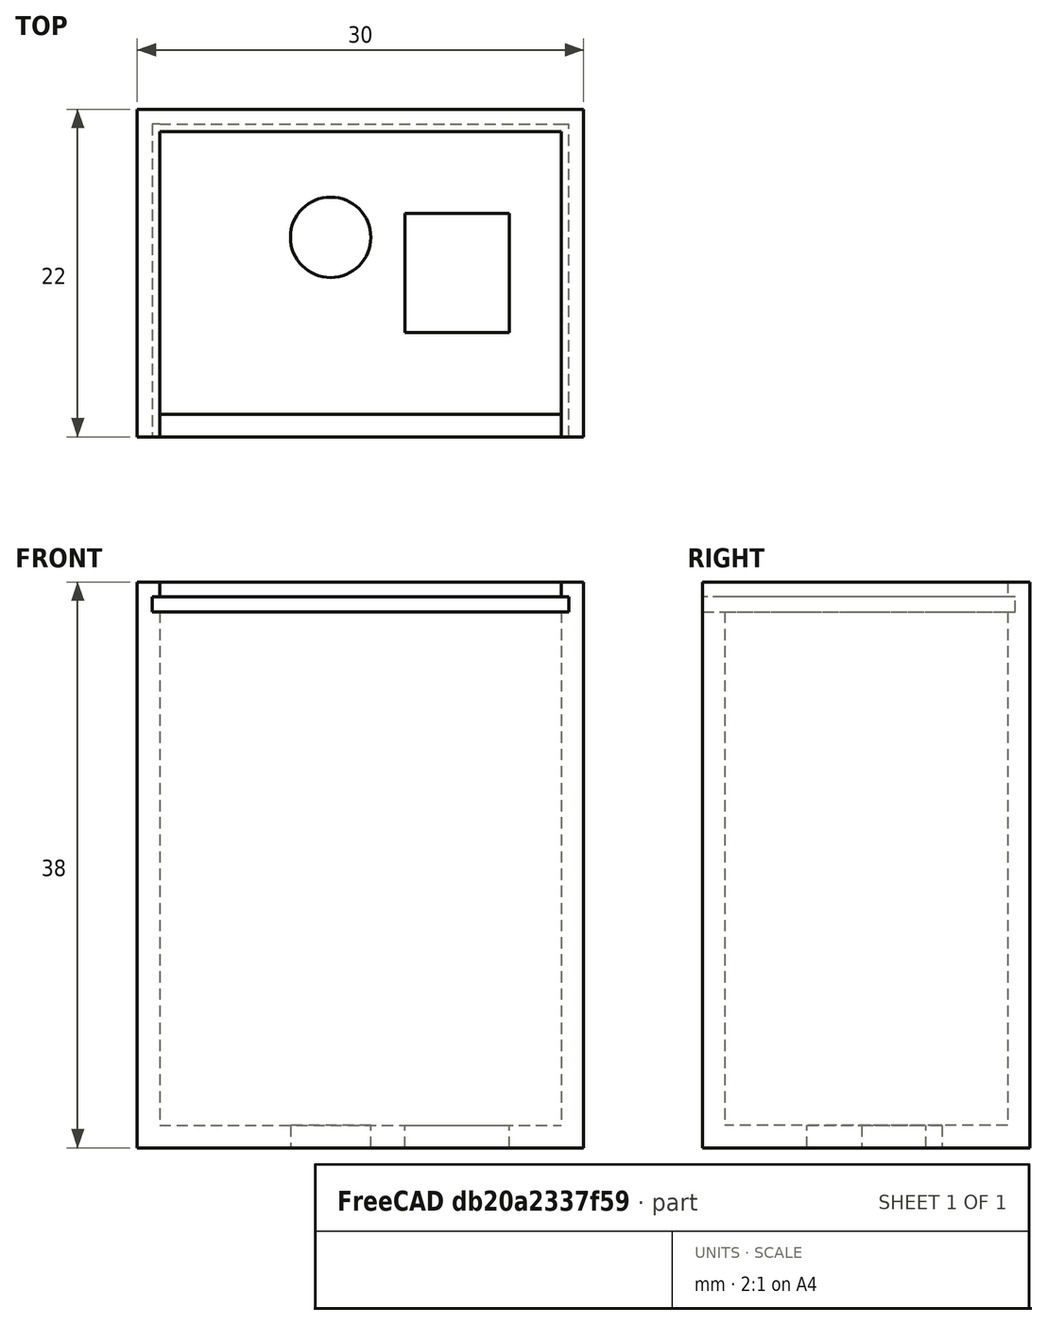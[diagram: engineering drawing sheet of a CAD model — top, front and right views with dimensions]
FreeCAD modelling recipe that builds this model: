
FCSTD DOCUMENT  (FreeCAD 0.18R4 (GitTag))
Label: IrDroid_Case_V2
License: All rights reserved
LicenseURL: http://en.wikipedia.org/wiki/All_rights_reserved
objects: Sketcher::SketchObject×9, PartDesign::Pocket×7, PartDesign::Pad×2, PartDesign::Body×2, Mesh::Feature×2, PartDesign::Mirrored×1, PartDesign::Fillet×1
note: 31 computed .brp shape members not serialized (recipe doc carries the construction recipe); baked Part::Feature solids carry a one-line shape summary decoded from their .brp

FEATURE [Sketcher::SketchObject] Sketch
  MapMode = 5
  Support = -> [XY_Plane]
  sketch-geometry (4):
    g0: LineSegment StartX=-15 StartY=11 StartZ=0 EndX=15 EndY=11 EndZ=0
    g1: LineSegment StartX=15 StartY=11 StartZ=0 EndX=15 EndY=-11 EndZ=0
    g2: LineSegment StartX=15 StartY=-11 StartZ=0 EndX=-15 EndY=-11 EndZ=0
    g3: LineSegment StartX=-15 StartY=-11 StartZ=0 EndX=-15 EndY=11 EndZ=0
  constraints (11):
    c: Coincident(g0,g1)
    c: Coincident(g1,g2)
    c: Coincident(g2,g3)
    c: Coincident(g3,g0)
    c: Horizontal(g0)
    c: Horizontal(g2)
    c: Vertical(g1)
    c: Vertical(g3)
    c: DistanceX(g0,g0) = 30
    c: DistanceY(g1,g1) = 22
    c: Symmetric(g0,g2,g-1)
FEATURE [PartDesign::Pad] Pad
  Length = 38
  Length2 = 100
  Profile = -> Sketch
  Type = 0
FEATURE [Sketcher::SketchObject] Sketch001
  ExternalGeometry = -> [Pad]
  MapMode = 5
  Placement = pos=(0,0,38) rot=(0,0,1;0rad)
  Support = -> [Pad]
  sketch-geometry (4):
    g0: LineSegment StartX=-13.5 StartY=9.5 StartZ=0 EndX=13.5 EndY=9.5 EndZ=0
    g1: LineSegment StartX=13.5 StartY=9.5 StartZ=0 EndX=13.5 EndY=-9.5 EndZ=0
    g2: LineSegment StartX=13.5 StartY=-9.5 StartZ=0 EndX=-13.5 EndY=-9.5 EndZ=0
    g3: LineSegment StartX=-13.5 StartY=-9.5 StartZ=0 EndX=-13.5 EndY=9.5 EndZ=0
  constraints (12):
    c: Coincident(g0,g1)
    c: Coincident(g1,g2)
    c: Coincident(g2,g3)
    c: Coincident(g3,g0)
    c: Horizontal(g0)
    c: Horizontal(g2)
    c: Vertical(g1)
    c: Vertical(g3)
    c: DistanceX(g0,g0) = 27
    c: DistanceY(g1,g1) = 19
    c: DistanceX(g0,g-4) = 1.5
    c: DistanceY(g0,g-4) = 1.5
FEATURE [PartDesign::Pocket] Pocket
  BaseFeature = -> Pad
  Length = 36.5
  Length2 = 100
  Profile = -> Sketch001
  Type = 0
FEATURE [Sketcher::SketchObject] Sketch002
  ExternalGeometry = -> [Pocket]
  MapMode = 5
  Placement = pos=(0,0,0) rot=(1,0,0;3.14159rad)
  Support = -> [Pocket]
  sketch-geometry (5):
    g0: LineSegment StartX=10 StartY=-4 StartZ=0 EndX=3 EndY=-4 EndZ=0
    g1: LineSegment StartX=3 StartY=-4 StartZ=0 EndX=3 EndY=4 EndZ=0
    g2: LineSegment StartX=3 StartY=4 StartZ=0 EndX=10 EndY=4 EndZ=0
    g3: LineSegment StartX=10 StartY=4 StartZ=0 EndX=10 EndY=-4 EndZ=0
    g4: Circle CenterX=-2 CenterY=-2.4 CenterZ=0 NormalX=0 NormalY=0 NormalZ=1 AngleXU=0 Radius=2.7
  constraints (15):
    c: Coincident(g0,g1)
    c: Coincident(g1,g2)
    c: Coincident(g2,g3)
    c: Coincident(g3,g0)
    c: Horizontal(g0)
    c: Horizontal(g2)
    c: Vertical(g1)
    c: Vertical(g3)
    c: DistanceY(g3,g3) = 8
    c: DistanceX(g2,g2) = 7
    c: DistanceY(g0,g-4) = -7
    c: DistanceX(g0,g-4) = 12
    c: Radius(g4) = 2.7
    c: DistanceX(g4,g0) = 12
    c: DistanceY(g-4,g4) = 8.6
FEATURE [PartDesign::Pocket] Pocket001
  BaseFeature = -> Pocket
  Length = 5
  Length2 = 100
  Profile = -> Sketch002
  Type = 1
FEATURE [Sketcher::SketchObject] Sketch003
  ExternalGeometry = -> [Pocket001]
  MapMode = 5
  Placement = pos=(0,-11,0) rot=(1,0,0;1.5708rad)
  Support = -> [Pocket001]
  sketch-geometry (4):
    g0: LineSegment StartX=-13.5 StartY=38 StartZ=0 EndX=13.5 EndY=38 EndZ=0
    g1: LineSegment StartX=13.5 StartY=38 StartZ=0 EndX=13.5 EndY=36 EndZ=0
    g2: LineSegment StartX=13.5 StartY=36 StartZ=0 EndX=-13.5 EndY=36 EndZ=0
    g3: LineSegment StartX=-13.5 StartY=36 StartZ=0 EndX=-13.5 EndY=38 EndZ=0
  constraints (12):
    c: Coincident(g0,g1)
    c: Coincident(g1,g2)
    c: Coincident(g2,g3)
    c: Coincident(g3,g0)
    c: Horizontal(g0)
    c: Horizontal(g2)
    c: Vertical(g1)
    c: Vertical(g3)
    c: DistanceY(g1,g1) = 2
    c: DistanceY(g0,g-5) = 0
    c: DistanceX(g1,g-5) = 1.5
    c: DistanceX(g-4,g2) = 1.5
FEATURE [PartDesign::Pocket] Pocket002
  BaseFeature = -> Pocket001
  Length = 1.5
  Length2 = 100
  Profile = -> Sketch003
  Type = 0
FEATURE [Sketcher::SketchObject] Sketch004
  ExternalGeometry = -> [Pocket002]
  MapMode = 5
  Placement = pos=(13.5,0,0) rot=(0.57735,-0.57735,-0.57735;2.0944rad)
  Support = -> [Pocket002]
  sketch-geometry (4):
    g0: LineSegment StartX=-10 StartY=37 StartZ=0 EndX=11 EndY=37 EndZ=0
    g1: LineSegment StartX=11 StartY=37 StartZ=0 EndX=11 EndY=36 EndZ=0
    g2: LineSegment StartX=11 StartY=36 StartZ=0 EndX=-10 EndY=36 EndZ=0
    g3: LineSegment StartX=-10 StartY=36 StartZ=0 EndX=-10 EndY=37 EndZ=0
  constraints (12):
    c: Coincident(g0,g1)
    c: Coincident(g1,g2)
    c: Coincident(g2,g3)
    c: Coincident(g3,g0)
    c: Horizontal(g0)
    c: Horizontal(g2)
    c: Vertical(g1)
    c: Vertical(g3)
    c: DistanceY(g1,g1) = 1
    c: DistanceX(g-4,g0) = -0.5
    c: DistanceY(g-4,g0) = 35.5
    c: DistanceX(g0,g0) = 21
FEATURE [PartDesign::Pocket] Pocket003
  BaseFeature = -> Pocket002
  Length = 0.5
  Length2 = 100
  Profile = -> Sketch004
  Type = 0
FEATURE [PartDesign::Mirrored] Mirrored
  BaseFeature = -> Pocket003
  MirrorPlane = -> YZ_Plane
  Originals = -> [Pocket003]
FEATURE [Sketcher::SketchObject] Sketch006
  MapMode = 5
  Support = -> [XY_Plane001]
  sketch-geometry (4):
    g0: LineSegment StartX=-13.9 StartY=9.9 StartZ=0 EndX=13.9 EndY=9.9 EndZ=0
    g1: LineSegment StartX=13.9 StartY=9.9 StartZ=0 EndX=13.9 EndY=-9.9 EndZ=0
    g2: LineSegment StartX=13.9 StartY=-9.9 StartZ=0 EndX=-13.9 EndY=-9.9 EndZ=0
    g3: LineSegment StartX=-13.9 StartY=-9.9 StartZ=0 EndX=-13.9 EndY=9.9 EndZ=0
  constraints (11):
    c: Coincident(g0,g1)
    c: Coincident(g1,g2)
    c: Coincident(g2,g3)
    c: Coincident(g3,g0)
    c: Horizontal(g0)
    c: Horizontal(g2)
    c: Vertical(g1)
    c: Vertical(g3)
    c: DistanceX(g0,g0) = 27.8
    c: DistanceY(g1,g1) = 19.8
    c: Symmetric(g0,g2,g-1)
FEATURE [PartDesign::Pad] Pad001
  Length = 0.8
  Length2 = 100
  Profile = -> Sketch006
  Type = 0
FEATURE [Sketcher::SketchObject] Sketch007
  ExternalGeometry = -> [Pad001]
  MapMode = 5
  Placement = pos=(0,0,0.8) rot=(0,0,1;0rad)
  Support = -> [Pad001]
  sketch-geometry (4):
    g0: LineSegment StartX=-6.5 StartY=9.9 StartZ=0 EndX=5.5 EndY=9.9 EndZ=0
    g1: LineSegment StartX=5.5 StartY=9.9 StartZ=0 EndX=5.5 EndY=5.4 EndZ=0
    g2: LineSegment StartX=5.5 StartY=5.4 StartZ=0 EndX=-6.5 EndY=5.4 EndZ=0
    g3: LineSegment StartX=-6.5 StartY=5.4 StartZ=0 EndX=-6.5 EndY=9.9 EndZ=0
  constraints (12):
    c: Coincident(g0,g1)
    c: Coincident(g1,g2)
    c: Coincident(g2,g3)
    c: Coincident(g3,g0)
    c: Horizontal(g0)
    c: Horizontal(g2)
    c: Vertical(g1)
    c: Vertical(g3)
    c: DistanceY(g1,g1) = 4.5
    c: DistanceX(g2,g2) = 12
    c: DistanceX(g2,g-1) = 6.5
    c: DistanceY(g0,g-3) = 0
FEATURE [PartDesign::Pocket] Pocket005
  BaseFeature = -> Pad001
  Length = 5
  Length2 = 100
  Profile = -> Sketch007
  Type = 1
FEATURE [Sketcher::SketchObject] Sketch008
  ExternalGeometry = -> [Pocket005]
  MapMode = 5
  Placement = pos=(0,0,0.8) rot=(0,0,1;0rad)
  Support = -> [Pocket005]
  sketch-geometry (4):
    g0: LineSegment StartX=-2.5 StartY=-4.4 StartZ=0 EndX=2.5 EndY=-4.4 EndZ=0
    g1: LineSegment StartX=2.5 StartY=-4.4 StartZ=0 EndX=2.5 EndY=-5.9 EndZ=0
    g2: LineSegment StartX=2.5 StartY=-5.9 StartZ=0 EndX=-2.5 EndY=-5.9 EndZ=0
    g3: LineSegment StartX=-2.5 StartY=-5.9 StartZ=0 EndX=-2.5 EndY=-4.4 EndZ=0
  constraints (12):
    c: Coincident(g0,g1)
    c: Coincident(g1,g2)
    c: Coincident(g2,g3)
    c: Coincident(g3,g0)
    c: Horizontal(g0)
    c: Horizontal(g2)
    c: Vertical(g1)
    c: Vertical(g3)
    c: DistanceX(g0,g0) = 5
    c: DistanceY(g1,g1) = 1.5
    c: DistanceX(g2,g-1) = 2.5
    c: DistanceY(g-3,g1) = 4
FEATURE [PartDesign::Pocket] Pocket006
  BaseFeature = -> Pocket005
  Length = 5
  Length2 = 100
  Profile = -> Sketch008
  Type = 1
FEATURE [Sketcher::SketchObject] Sketch009
  ExternalGeometry = -> [Mirrored]
  MapMode = 5
  Placement = pos=(0,9.5,0) rot=(1,0,0;1.5708rad)
  Support = -> [Mirrored]
  sketch-geometry (4):
    g0: LineSegment StartX=-13.5 StartY=37 StartZ=0 EndX=13.5 EndY=37 EndZ=0
    g1: LineSegment StartX=13.5 StartY=37 StartZ=0 EndX=13.5 EndY=36 EndZ=0
    g2: LineSegment StartX=13.5 StartY=36 StartZ=0 EndX=-13.5 EndY=36 EndZ=0
    g3: LineSegment StartX=-13.5 StartY=36 StartZ=0 EndX=-13.5 EndY=37 EndZ=0
  constraints (12):
    c: Coincident(g0,g1)
    c: Coincident(g1,g2)
    c: Coincident(g2,g3)
    c: Coincident(g3,g0)
    c: Horizontal(g0)
    c: Horizontal(g2)
    c: Vertical(g1)
    c: Vertical(g3)
    c: DistanceY(g1,g1) = 1
    c: DistanceX(g0,g0) = 27
    c: DistanceY(g-1,g0) = 37
    c: DistanceX(g0,g-1) = 13.5
FEATURE [PartDesign::Pocket] Pocket007
  BaseFeature = -> Mirrored
  Length = 0.5
  Length2 = 100
  Profile = -> Sketch009
  Type = 0
FEATURE [PartDesign::Body] Body  label="Case"
  Group = -> [Sketch,Pad,Sketch001,Pocket,Sketch002,Pocket001,Sketch003,Pocket002,Sketch004,Pocket003,Mirrored,Sketch009,Pocket007]
  Origin = -> Origin
  Tip = -> Pocket007
FEATURE [PartDesign::Fillet] Fillet
  Base = -> Pocket006 [Edge5,Edge1,Edge8,Edge10,Edge11,Edge23,Edge9,Edge7,Edge6,Edge19,Edge18,Edge20,Edge21,Edge22,Edge16,Edge3]
  BaseFeature = -> Pocket006
  Radius = 0.6
FEATURE [PartDesign::Body] Body001  label="Top"
  Group = -> [Sketch006,Pad001,Sketch007,Pocket005,Sketch008,Pocket006,Fillet]
  Origin = -> Origin001
  Tip = -> Fillet
FEATURE [Mesh::Feature] Mesh001  label="Case001"
FEATURE [Mesh::Feature] Mesh  label="Top001"
